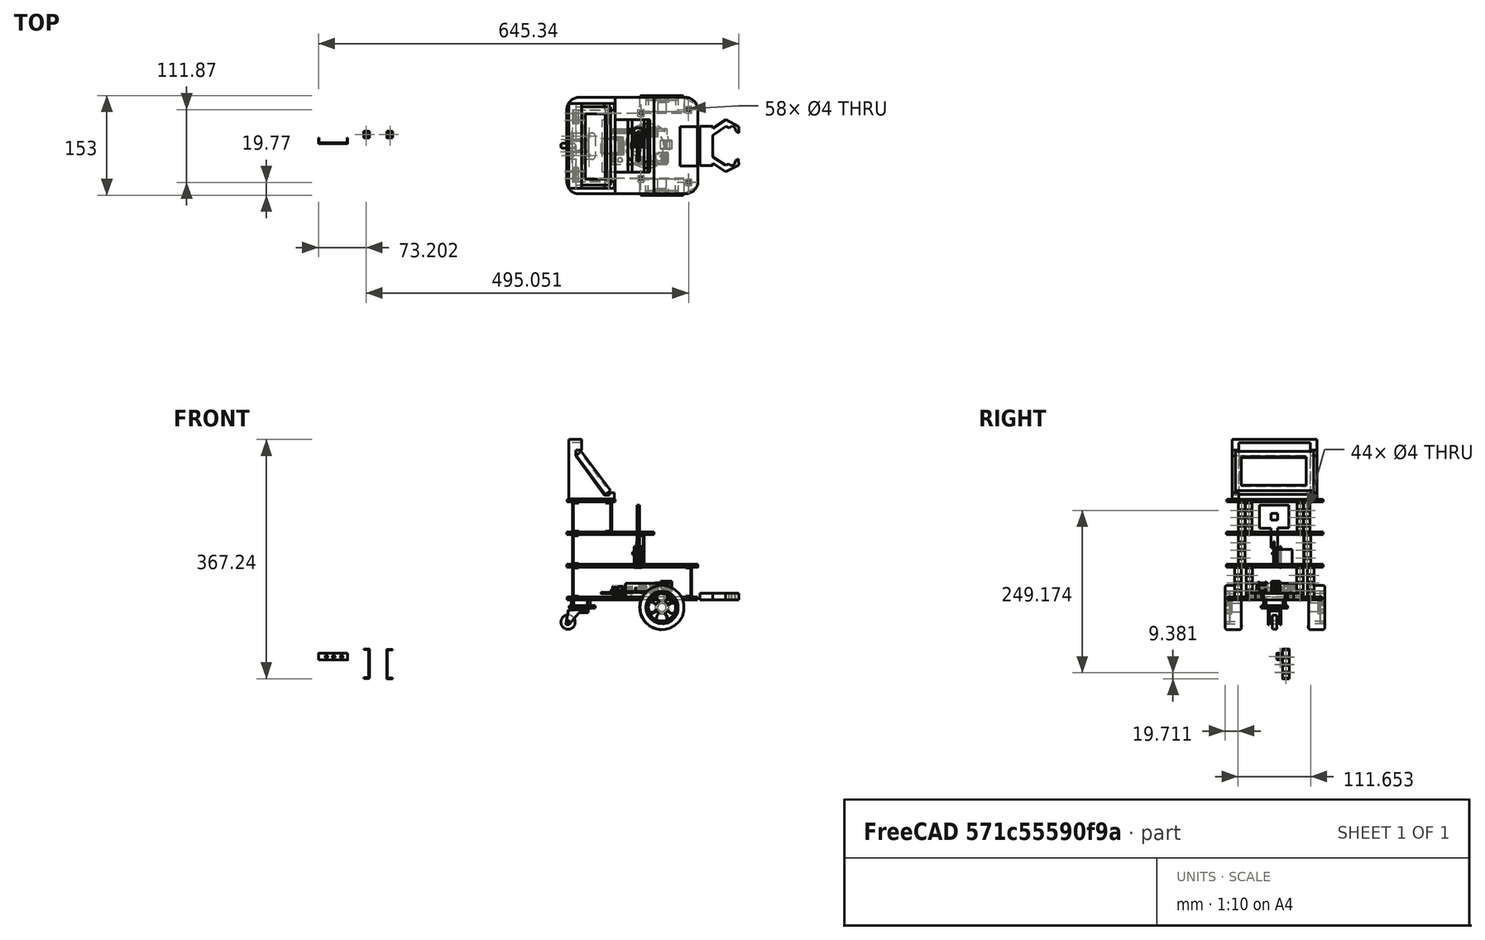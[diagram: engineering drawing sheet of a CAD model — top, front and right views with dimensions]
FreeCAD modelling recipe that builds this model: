
FCSTD DOCUMENT
Label: robot
objects: Part::Feature×53, Part::Cylinder×29, Part::Cut×29, Sketcher::SketchObject×12, PartDesign::Pad×11, App::DocumentObjectGroup×11, Part::MultiFuse×7, Part::Box×7, Part::Fillet×3, Mesh::Feature×1
note: 162 computed .brp shape members not serialized (recipe doc carries the construction recipe); baked Part::Feature solids carry a one-line shape summary decoded from their .brp

FEATURE [Sketcher::SketchObject] Sketch
  sketch-geometry (28):
    g0: LineSegment StartX=-101.13 StartY=50 StartZ=0 EndX=56.3229 EndY=50 EndZ=0
    g1: LineSegment StartX=56.3229 StartY=-50 StartZ=0 EndX=-101.13 EndY=-50 EndZ=0
    g2: LineSegment StartX=-123.405 StartY=-27.7251 StartZ=0 EndX=-123.405 EndY=27.7251 EndZ=0
    g3: ArcOfCircle CenterX=-101.13 CenterY=27.7251 CenterZ=0 NormalX=0 NormalY=0 NormalZ=1 Radius=22.2749 StartAngle=1.5708 EndAngle=3.14159
    g4: ArcOfCircle CenterX=-101.13 CenterY=-27.7251 CenterZ=0 NormalX=0 NormalY=0 NormalZ=1 Radius=22.2749 StartAngle=3.14159 EndAngle=4.71239
    g5: LineSegment StartX=6.49 StartY=27.5 StartZ=0 EndX=26.49 EndY=27.5 EndZ=0
    g6: LineSegment StartX=26.49 StartY=27.5 StartZ=0 EndX=26.49 EndY=22.5 EndZ=0
    g7: LineSegment StartX=26.49 StartY=22.5 StartZ=0 EndX=6.49 EndY=22.5 EndZ=0
    g8: LineSegment StartX=6.49 StartY=22.5 StartZ=0 EndX=6.49 EndY=27.5 EndZ=0
    g9: LineSegment StartX=6.49 StartY=-22.5 StartZ=0 EndX=26.49 EndY=-22.5 EndZ=0
    g10: LineSegment StartX=26.49 StartY=-22.5 StartZ=0 EndX=26.49 EndY=-27.5 EndZ=0
    g11: LineSegment StartX=26.49 StartY=-27.5 StartZ=0 EndX=6.49 EndY=-27.5 EndZ=0
    g12: LineSegment StartX=6.49 StartY=-27.5 StartZ=0 EndX=6.49 EndY=-22.5 EndZ=0
    g13: Circle CenterX=-115.043 CenterY=15 CenterZ=0 NormalX=0 NormalY=0 NormalZ=1 Radius=2
    g14: Circle CenterX=-115.043 CenterY=-15 CenterZ=0 NormalX=0 NormalY=0 NormalZ=1 Radius=2
    g15: Circle CenterX=-90.0431 CenterY=15 CenterZ=0 NormalX=0 NormalY=0 NormalZ=1 Radius=2
    g16: Circle CenterX=-90.0431 CenterY=-15 CenterZ=0 NormalX=0 NormalY=0 NormalZ=1 Radius=2
    g17: Circle CenterX=-109.936 CenterY=-38.9718 CenterZ=0 NormalX=0 NormalY=0 NormalZ=1 Radius=2
    g18: Circle CenterX=-109.936 CenterY=38.9718 CenterZ=0 NormalX=0 NormalY=0 NormalZ=1 Radius=2
    g19: Circle CenterX=62.653 CenterY=55.5053 CenterZ=0 NormalX=0 NormalY=0 NormalZ=1 Radius=2
    g20: Circle CenterX=62.6558 CenterY=-55.7448 CenterZ=0 NormalX=0 NormalY=0 NormalZ=1 Radius=2
    g21: LineSegment StartX=56.3229 StartY=50 StartZ=0 EndX=56.3229 EndY=73.4411 EndZ=0
    g22: LineSegment StartX=56.3229 StartY=73.4411 StartZ=0 EndX=71.7147 EndY=65.2083 EndZ=0
    g23: LineSegment StartX=76.7067 StartY=56.8801 StartZ=0 EndX=76.7456 EndY=-57.0322 EndZ=0
    g24: LineSegment StartX=71.4963 StartY=-65.4994 StartZ=0 EndX=56.3229 EndY=-73.027 EndZ=0
    g25: LineSegment StartX=56.3229 StartY=-73.027 StartZ=0 EndX=56.3229 EndY=-50 EndZ=0
    g26: ArcOfCircle CenterX=67.2972 CenterY=-57.0354 CenterZ=0 NormalX=0 NormalY=0 NormalZ=1 Radius=9.44836 StartAngle=5.17292 EndAngle=6.28353
    g27: ArcOfCircle CenterX=67.2584 CenterY=56.8768 CenterZ=0 NormalX=0 NormalY=0 NormalZ=1 Radius=9.44836 StartAngle=0.000340973 EndAngle=1.07963
  constraints (66):
    c: Horizontal(g0)
    c: Horizontal(g1)
    c: Vertical(g2)
    c: Tangent(g0,g3)
    c: Tangent(g2,g3)
    c: Tangent(g1,g4)
    c: Tangent(g2,g4)
    c: Equal(g4,g3)
    c: Symmetric(g3,g4,g4)
    c: Coincident(g5,g6)
    c: Coincident(g6,g7)
    c: Coincident(g7,g8)
    c: Coincident(g8,g5)
    c: Horizontal(g5)
    c: Horizontal(g7)
    c: Vertical(g6)
    c: Vertical(g8)
    c: Coincident(g9,g10)
    c: Coincident(g10,g11)
    c: Coincident(g11,g12)
    c: Coincident(g12,g9)
    c: Horizontal(g9)
    c: Horizontal(g11)
    c: Vertical(g10)
    c: Vertical(g12)
    c: Equal(g9,g7)
    c: Equal(g10,g6)
    c: DistanceY(g9,g6) = 45
    c: Symmetric(g7,g9,g4)
    c: DistanceY(g11,g9) = 5
    c: Distance(g9,g2) = 130
    c: DistanceX(g5,g5) = 20
    c: Equal(g14,g13)
    c: Equal(g13,g15)
    c: Equal(g15,g16)
    c: Equal(g16,g17)
    c: Equal(g17,g18)
    c: Equal(g18,g19)
    c: Equal(g19,g20)
    c: Radius(g16) = 2
    c: Symmetric(g14,g13,g4)
    c: Symmetric(g15,g16,g4)
    c: Symmetric(g18,g17,g4)
    c: Symmetric(g20,g19,g4)
    c: DistanceY(g13,g14) = -30
    c: DistanceX(g15,g13) = -25
    c: DistanceY(g16,g15) = 30
    c: DistanceX(g14) = -115.043
    c: DistanceX(g17) = -109.936
    c: DistanceY(g17,g18) = 77.9436
    c: Coincident(g21,g0)
    c: Coincident(g21,g22)
    c: Coincident(g24,g25)
    c: Coincident(g25,g1)
    c: Tangent(g23,g26)
    c: Tangent(g24,g26)
    c: Tangent(g22,g27)
    c: Tangent(g23,g27)
    c: Equal(g27,g26)
    c: Symmetric(g21,g24,g3)
    c: Symmetric(g26,g27,g3)
    c: DistanceY(g0) = 50
    c: DistanceY(g0,g1) = -100
    c: Symmetric(g20,g19,g3)
    c: Vertical(g25)
    c: Vertical(g21)
FEATURE [Sketcher::SketchObject] Sketch001
  sketch-geometry (31):
    g0: LineSegment StartX=-104.318 StartY=74.4003 StartZ=0 EndX=57.597 EndY=74.4003 EndZ=0
    g1: LineSegment StartX=57.7487 StartY=-73.8607 StartZ=0 EndX=-104.318 EndY=-73.8607 EndZ=0
    g2: LineSegment StartX=-124.085 StartY=-54.0935 StartZ=0 EndX=-124.085 EndY=54.6331 EndZ=0
    g3: LineSegment [constr] StartX=-124.085 StartY=-0.458382 StartZ=0 EndX=-29.7491 EndY=-0.458382 EndZ=0
    g4: Circle CenterX=-110.299 CenterY=39.0839 CenterZ=0 NormalX=0 NormalY=0 NormalZ=1 Radius=2
    g5: Circle CenterX=-109.764 CenterY=-38.9049 CenterZ=0 NormalX=0 NormalY=0 NormalZ=1 Radius=2
    g6: Circle CenterX=62.7977 CenterY=55.4219 CenterZ=0 NormalX=0 NormalY=0 NormalZ=1 Radius=2
    g7: Circle CenterX=62.9826 CenterY=-55.9466 CenterZ=0 NormalX=0 NormalY=0 NormalZ=1 Radius=2
    g8: ArcOfCircle CenterX=-104.318 CenterY=54.6331 CenterZ=0 NormalX=0 NormalY=0 NormalZ=1 Radius=19.7672 StartAngle=1.5708 EndAngle=3.14159
    g9: ArcOfCircle CenterX=-104.318 CenterY=-54.0935 CenterZ=0 NormalX=0 NormalY=0 NormalZ=1 Radius=19.7672 StartAngle=3.14159 EndAngle=4.71239
    g10: ArcOfCircle CenterX=57.597 CenterY=54.6331 CenterZ=0 NormalX=0 NormalY=0 NormalZ=1 Radius=19.7672 StartAngle=6.22162 EndAngle=7.85398
    g11: ArcOfCircle CenterX=57.7487 CenterY=-54.0935 CenterZ=0 NormalX=0 NormalY=0 NormalZ=1 Radius=19.7672 StartAngle=4.71239 EndAngle=6.14475
    g12: LineSegment StartX=77.3268 StartY=29.3887 StartZ=0 EndX=50.0396 EndY=29.3887 EndZ=0
    g13: LineSegment StartX=50.0396 StartY=29.3887 StartZ=0 EndX=50.0396 EndY=-30.714 EndZ=0
    g14: LineSegment StartX=77.3268 StartY=-56.8212 StartZ=0 EndX=77.3268 EndY=-30.714 EndZ=0
    g15: LineSegment StartX=77.3268 StartY=29.3887 StartZ=0 EndX=77.3268 EndY=53.4168 EndZ=0
    g16: Circle CenterX=-110.008 CenterY=-50.2945 CenterZ=0 NormalX=0 NormalY=0 NormalZ=1 Radius=2
    g17: Circle CenterX=-110.008 CenterY=49.3777 CenterZ=0 NormalX=0 NormalY=0 NormalZ=1 Radius=2
    g18: Circle CenterX=-10.1147 CenterY=50.2419 CenterZ=0 NormalX=0 NormalY=0 NormalZ=1 Radius=2
    g19: Circle CenterX=-10.1344 CenterY=-50.6043 CenterZ=0 NormalX=0 NormalY=0 NormalZ=1 Radius=2
    g20: LineSegment StartX=-29.7491 StartY=40.2702 StartZ=0 EndX=-23.9444 EndY=40.2702 EndZ=0
    g21: LineSegment StartX=-23.9444 StartY=40.2702 StartZ=0 EndX=-23.9444 EndY=-40.2702 EndZ=0
    g22: LineSegment StartX=-23.9444 StartY=-40.2702 StartZ=0 EndX=-29.7491 EndY=-40.2702 EndZ=0
    g23: LineSegment StartX=-29.7491 StartY=-40.2702 StartZ=0 EndX=-29.7491 EndY=40.2702 EndZ=0
    g24: LineSegment StartX=-5.44191 StartY=40.2702 StartZ=0 EndX=0.362807 EndY=40.2702 EndZ=0
    g25: LineSegment StartX=0.362807 StartY=40.2702 StartZ=0 EndX=0.362807 EndY=-40.2702 EndZ=0
    g26: LineSegment StartX=0.362807 StartY=-40.2702 StartZ=0 EndX=-5.44191 EndY=-40.2702 EndZ=0
    g27: LineSegment StartX=-5.44191 StartY=-40.2702 StartZ=0 EndX=-5.44191 EndY=40.2702 EndZ=0
    g28: LineSegment [constr] StartX=-23.9444 StartY=-0.458382 StartZ=0 EndX=-5.44191 EndY=-0.458382 EndZ=0
    g29: LineSegment [constr] StartX=50.0396 StartY=-0.458382 StartZ=0 EndX=76.3643 EndY=-0.458382 EndZ=0
    g30: LineSegment StartX=77.3268 StartY=-30.714 StartZ=0 EndX=50.0396 EndY=-30.714 EndZ=0
  constraints (45):
    c: Horizontal(g0)
    c: Horizontal(g1)
    c: Vertical(g2)
    c: PointOnObject(g3,g2)
    c: Equal(g5,g4)
    c: Equal(g4,g6)
    c: Equal(g6,g7)
    c: Radius(g5) = 2
    c: Tangent(g0,g8)
    c: Tangent(g2,g8)
    c: Tangent(g1,g9)
    c: Tangent(g2,g9)
    c: Tangent(g0,g10)
    c: Tangent(g1,g11)
    c: Horizontal(g12)
    c: Coincident(g12,g13)
    c: Vertical(g13)
    c: Coincident(g14,g11)
    c: Vertical(g14)
    c: Coincident(g15,g12)
    c: Coincident(g15,g10)
    c: Vertical(g15)
    c: Equal(g16,g17)
    c: Radius(g16) = 2
    c: Radius(g18) = 2
    c: Coincident(g20,g21)
    c: Coincident(g21,g22)
    c: Coincident(g22,g23)
    c: Coincident(g23,g20)
    c: Horizontal(g20)
    c: Horizontal(g22)
    c: Coincident(g24,g25)
    c: Coincident(g25,g26)
    c: Coincident(g26,g27)
    c: Coincident(g27,g24)
    c: Horizontal(g24)
    c: Horizontal(g26)
    c: Symmetric(g16,g17,g3)
    c: Tangent(g3,g28)
    c: PointOnObject(g29,g13)
    c: Tangent(g28,g29)
    c: PointOnObject(g28,g27)
    c: Coincident(g30,g14)
    c: Coincident(g30,g13)
    c: Horizontal(g30)
FEATURE [PartDesign::Pad] Pad001
  Length = 4
  MirroredExtent = false
  Placement = pos=(0,0,50) rot=(0,0,1;0rad)
  Sketch = -> Sketch001
FEATURE [Sketcher::SketchObject] Sketch002
  sketch-geometry (18):
    g0: LineSegment StartX=-104.405 StartY=74.3817 StartZ=0 EndX=9.85074 EndY=74.3817 EndZ=0
    g1: LineSegment StartX=9.85074 StartY=74.3817 StartZ=0 EndX=9.85074 EndY=-73.7972 EndZ=0
    g2: LineSegment StartX=9.85074 StartY=-73.7972 StartZ=0 EndX=-104.405 EndY=-73.7972 EndZ=0
    g3: LineSegment StartX=-123.988 StartY=-54.214 StartZ=0 EndX=-123.988 EndY=54.7984 EndZ=0
    g4: ArcOfCircle CenterX=-104.405 CenterY=54.7984 CenterZ=0 NormalX=0 NormalY=0 NormalZ=1 Radius=19.5832 StartAngle=1.5708 EndAngle=3.14159
    g5: ArcOfCircle CenterX=-104.405 CenterY=-54.214 CenterZ=0 NormalX=0 NormalY=0 NormalZ=1 Radius=19.5832 StartAngle=3.14159 EndAngle=4.71239
    g6: Circle CenterX=-109.932 CenterY=49.3917 CenterZ=0 NormalX=0 NormalY=0 NormalZ=1 Radius=2
    g7: Circle CenterX=-110.012 CenterY=-50.1232 CenterZ=0 NormalX=0 NormalY=0 NormalZ=1 Radius=2
    g8: Circle CenterX=-9.94777 CenterY=50.1271 CenterZ=0 NormalX=0 NormalY=0 NormalZ=1 Radius=2
    g9: Circle CenterX=-10.198 CenterY=-50.2781 CenterZ=0 NormalX=0 NormalY=0 NormalZ=1 Radius=2
    g10: LineSegment StartX=-69.6455 StartY=40.3214 StartZ=0 EndX=3.40336 EndY=40.3214 EndZ=0
    g11: LineSegment StartX=3.40336 StartY=40.3214 StartZ=0 EndX=3.40336 EndY=-40.303 EndZ=0
    g12: LineSegment StartX=3.40336 StartY=-40.303 StartZ=0 EndX=-69.6455 EndY=-40.303 EndZ=0
    g13: LineSegment StartX=-69.6455 StartY=-40.303 StartZ=0 EndX=-69.6455 EndY=40.3214 EndZ=0
    g14: Circle CenterX=-109.839 CenterY=39.7373 CenterZ=0 NormalX=0 NormalY=0 NormalZ=1 Radius=2
    g15: Circle CenterX=-110.415 CenterY=-39.9994 CenterZ=0 NormalX=0 NormalY=0 NormalZ=1 Radius=2
    g16: Circle CenterX=-59.5193 CenterY=-50.2572 CenterZ=0 NormalX=0 NormalY=0 NormalZ=1 Radius=2
    g17: Circle CenterX=-60.2629 CenterY=49.9665 CenterZ=0 NormalX=0 NormalY=0 NormalZ=1 Radius=2
  constraints (27):
    c: Coincident(g0,g1)
    c: Coincident(g1,g2)
    c: Horizontal(g0)
    c: Horizontal(g2)
    c: Vertical(g1)
    c: Vertical(g3)
    c: Tangent(g0,g4)
    c: Tangent(g3,g4)
    c: Tangent(g2,g5)
    c: Tangent(g3,g5)
    c: Equal(g4,g5)
    c: Equal(g6,g7)
    c: Equal(g7,g9)
    c: Equal(g9,g8)
    c: Radius(g6) = 2
    c: Coincident(g10,g11)
    c: Coincident(g11,g12)
    c: Coincident(g12,g13)
    c: Coincident(g13,g10)
    c: Horizontal(g10)
    c: Horizontal(g12)
    c: Vertical(g11)
    c: Vertical(g13)
    c: Equal(g15,g14)
    c: Equal(g14,g17)
    c: Equal(g17,g16)
    c: Radius(g15) = 2
FEATURE [PartDesign::Pad] Pad002
  Length = 4
  MirroredExtent = false
  Placement = pos=(0,0,100) rot=(0,0,1;0rad)
  Sketch = -> Sketch002
FEATURE [Sketcher::SketchObject] Sketch003
  sketch-geometry (12):
    g0: ArcOfCircle CenterX=-105.074 CenterY=55.6821 CenterZ=0 NormalX=0 NormalY=0 NormalZ=1 Radius=18.6332 StartAngle=1.60655 EndAngle=3.14159
    g1: ArcOfCircle CenterX=-105.346 CenterY=-55.3418 CenterZ=0 NormalX=0 NormalY=0 NormalZ=1 Radius=18.3958 StartAngle=3.20271 EndAngle=4.69093
    g2: LineSegment StartX=-50.0043 StartY=74.3033 StartZ=0 EndX=-50.0043 EndY=-73.7333 EndZ=0
    g3: LineSegment StartX=-105.74 StartY=74.3033 StartZ=0 EndX=-50.0043 EndY=74.3033 EndZ=0
    g4: LineSegment StartX=-105.741 StartY=-73.7333 StartZ=0 EndX=-50.0043 EndY=-73.7333 EndZ=0
    g5: Circle CenterX=-109.743 CenterY=39.5908 CenterZ=0 NormalX=0 NormalY=0 NormalZ=1 Radius=2
    g6: Circle CenterX=-110.279 CenterY=-40.0459 CenterZ=0 NormalX=0 NormalY=0 NormalZ=1 Radius=2
    g7: Circle CenterX=-60.203 CenterY=49.9128 CenterZ=0 NormalX=0 NormalY=0 NormalZ=1 Radius=2
    g8: Circle CenterX=-59.3002 CenterY=-50.3702 CenterZ=0 NormalX=0 NormalY=0 NormalZ=1 Radius=2
    g9: Circle CenterX=-116.132 CenterY=9.74953 CenterZ=0 NormalX=0 NormalY=0 NormalZ=1 Radius=2
    g10: Circle CenterX=-116.544 CenterY=-9.66085 CenterZ=0 NormalX=0 NormalY=0 NormalZ=1 Radius=2
    g11: LineSegment StartX=-123.707 StartY=55.6821 StartZ=0 EndX=-123.707 EndY=-56.4655 EndZ=0
  constraints (17):
    c: Coincident(g3,g0)
    c: Coincident(g3,g2)
    c: Coincident(g4,g1)
    c: Coincident(g4,g2)
    c: Equal(g6,g5)
    c: Equal(g5,g7)
    c: Equal(g7,g8)
    c: Radius(g6) = 2
    c: Horizontal(g3)
    c: Vertical(g2)
    c: Horizontal(g4)
    c: Equal(g10,g9)
    c: Radius(g9) = 2
    c: Coincident(g11,g0)
    c: Coincident(g11,g1)
    c: Vertical(g11)
    c: Tangent(g11,g0)
FEATURE [PartDesign::Pad] Pad003
  Length = 4
  MirroredExtent = false
  Placement = pos=(0,0,150) rot=(0,0,1;0rad)
  Sketch = -> Sketch003
FEATURE [Part::Cylinder] Cylinder005
  Angle = 360
  Height = 25
  Radius = 6.5
FEATURE [Part::Cylinder] Cylinder006
  Angle = 360
  Height = 10
  Radius = 10
FEATURE [Part::Cylinder] Cylinder010
  Angle = 360
  Height = 7
  Placement = pos=(0.664718,-16.3626,0) rot=(0,0,1;0rad)
  Radius = 8
FEATURE [Part::Cylinder] Cylinder011
  Angle = 360
  Height = 7
  Placement = pos=(16.4955,0.685902,0) rot=(0,0,1;0rad)
  Radius = 8
FEATURE [Part::Cylinder] Cylinder012
  Angle = 360
  Height = 7
  Placement = pos=(-16.3838,-1.44516,0) rot=(0,0,1;0rad)
  Radius = 8
FEATURE [Part::Cylinder] Cylinder013
  Angle = 360
  Height = 25
  Radius = 25
FEATURE [Part::Cylinder] Cylinder009
  Angle = 360
  Height = 7
  Placement = pos=(-0.248596,16.2122,0) rot=(0,0,1;0rad)
  Radius = 8
FEATURE [Part::MultiFuse] Fusion
  Placement = pos=(22,77,-12) rot=(1,0,0;1.5708rad)
  Shapes = -> [Cylinder006,Cylinder011,Cylinder012,Cylinder010,Cylinder009,Cylinder005]
FEATURE [Part::Cylinder] Cylinder014
  Angle = 360
  Height = 25
  Radius = 34
FEATURE [Part::Cylinder] Cylinder015
  Angle = 360
  Height = 25
  Radius = 21
FEATURE [Part::Cylinder] Cylinder016
  Angle = 360
  Height = 25
  Radius = 25
FEATURE [Part::Cut] Cut002
  Base = -> Cylinder016
  Placement = pos=(22,77,-12) rot=(1,0,0;1.5708rad)
  Tool = -> Cylinder015
FEATURE [Part::Fillet] Fillet
  Edges = 2 edges r=3: [Edge2,Edge3]
  Placement = pos=(22,77,-12) rot=(1,0,0;1.5708rad)
FEATURE [App::DocumentObjectGroup] Group  label="wheel"
  Group = -> [Cut002,Fusion,Fillet]
FEATURE [Part::Cylinder] Cylinder
  Angle = 360
  Height = 7
  Radius = 11
FEATURE [Part::Cylinder] Cylinder017
  Angle = 360
  Height = 7
  Radius = 2.5
FEATURE [Part::Cut] Cut
  Base = -> Cylinder
  Tool = -> Cylinder017
FEATURE [Part::Fillet] Fillet001
  Base = -> Cut
  Edges = 4 edges r=2: [Edge1,Edge3,Edge4,Edge5]
  Placement = pos=(-122,-3.4,-34.5) rot=(0,0.707107,0.707107;3.14159rad)
FEATURE [App::DocumentObjectGroup] Group001  label="wheel0"
  Group = -> [Cylinder017,Cylinder,Fillet001]
FEATURE [Sketcher::SketchObject] Sketch004
  sketch-geometry (11):
    g0: LineSegment StartX=-39.5249 StartY=-0.0489382 StartZ=0 EndX=-9.52487 EndY=-0.0489382 EndZ=0
    g1: LineSegment StartX=-9.52487 StartY=-0.0489382 StartZ=0 EndX=-5.3256 EndY=-21.3647 EndZ=0
    g2: LineSegment StartX=-6.46484 StartY=-22.7502 StartZ=0 EndX=-9.08519 EndY=-22.7502 EndZ=0
    g3: LineSegment StartX=-10.2117 StartY=-22.2424 StartZ=0 EndX=-25.3922 EndY=-5.06478 EndZ=0
    g4: LineSegment StartX=-27.2038 StartY=-4.24812 StartZ=0 EndX=-38.567 EndY=-4.24812 EndZ=0
    g5: LineSegment StartX=-39.5249 StartY=-3.29027 StartZ=0 EndX=-39.5249 EndY=-0.0489382 EndZ=0
    g6: ArcOfCircle CenterX=-6.46484 CenterY=-21.5891 CenterZ=0 NormalX=0 NormalY=0 NormalZ=1 Radius=1.16114 StartAngle=4.71239 EndAngle=6.4777
    g7: ArcOfCircle CenterX=-9.08519 CenterY=-21.2469 CenterZ=0 NormalX=0 NormalY=0 NormalZ=1 Radius=1.50333 StartAngle=3.86535 EndAngle=4.71239
    g8: ArcOfCircle CenterX=-27.2038 CenterY=-6.66574 CenterZ=0 NormalX=0 NormalY=0 NormalZ=1 Radius=2.41762 StartAngle=0.723759 EndAngle=1.5708
    g9: Circle CenterX=-8.87657 CenterY=-18.7194 CenterZ=0 NormalX=0 NormalY=0 NormalZ=1 Radius=2
    g10: ArcOfCircle CenterX=-38.567 CenterY=-3.29027 CenterZ=0 NormalX=0 NormalY=0 NormalZ=1 Radius=0.95785 StartAngle=3.14159 EndAngle=4.71239
  constraints (16):
    c: Horizontal(g0)
    c: Distance(g0) = 30
    c: Coincident(g1,g0)
    c: Horizontal(g2)
    c: Horizontal(g4)
    c: Coincident(g5,g0)
    c: Vertical(g5)
    c: Tangent(g1,g6)
    c: Tangent(g2,g6)
    c: Tangent(g2,g7)
    c: Tangent(g3,g7)
    c: Tangent(g3,g8)
    c: Tangent(g4,g8)
    c: Radius(g9) = 2
    c: Tangent(g4,g10)
    c: Tangent(g5,g10)
FEATURE [PartDesign::Pad] Pad004
  Length = 20
  MirroredExtent = false
  Placement = pos=(40,27,-2) rot=(0,0,1;0rad)
  Sketch = -> Sketch004
FEATURE [Part::Box] Box
  Height = 16
  Length = 40
  Width = 25
FEATURE [Part::Cut] Cut003
  Base = -> Pad004
  Placement = pos=(-90.7,-8,-42.5) rot=(0,0.707107,0.707107;3.14159rad)
  Tool = -> Box
FEATURE [App::DocumentObjectGroup] Group002  label="wl"
  Group = -> [Cut003]
FEATURE [Part::Fillet] Fillet002
  Edges = 2 edges r=3: [Edge2,Edge3]
  Placement = pos=(22.3,-76,-12) rot=(0,0.707107,0.707107;3.14159rad)
FEATURE [Part::MultiFuse] Fusion001
  Placement = pos=(22.3,-76,-12) rot=(0,0.707107,0.707107;3.14159rad)
  Shapes = -> [Cylinder006,Cylinder011,Cylinder012,Cylinder010,Cylinder009,Cylinder005]
FEATURE [Part::Cut] Cut004
  Base = -> Cylinder016
  Placement = pos=(22.3,-76,-12) rot=(0,0.707107,0.707107;3.14159rad)
  Tool = -> Cylinder015
FEATURE [App::DocumentObjectGroup] Group003  label="wheel01"
  Group = -> [Cut004,Fusion001,Fillet002]
FEATURE [App::DocumentObjectGroup] Group004
FEATURE [Sketcher::SketchObject] Sketch005  label="Sketch_plate"
  sketch-geometry (12):
    g0: LineSegment StartX=-114.888 StartY=19.7983 StartZ=0 EndX=-85.6217 EndY=19.7983 EndZ=0
    g1: LineSegment StartX=-80.1008 StartY=14.2774 StartZ=0 EndX=-80.1008 EndY=-15.4701 EndZ=0
    g2: LineSegment StartX=-85.6217 StartY=-20.991 StartZ=0 EndX=-114.888 EndY=-20.991 EndZ=0
    g3: LineSegment StartX=-120.409 StartY=-15.4701 StartZ=0 EndX=-120.409 EndY=14.2774 EndZ=0
    g4: Circle CenterX=-115.076 CenterY=14.931 CenterZ=0 NormalX=0 NormalY=0 NormalZ=1 Radius=2
    g5: Circle CenterX=-115.258 CenterY=-14.9052 CenterZ=0 NormalX=0 NormalY=0 NormalZ=1 Radius=2
    g6: Circle CenterX=-90.0087 CenterY=14.931 CenterZ=0 NormalX=0 NormalY=0 NormalZ=1 Radius=2
    g7: Circle CenterX=-89.8897 CenterY=-14.9413 CenterZ=0 NormalX=0 NormalY=0 NormalZ=1 Radius=2
    g8: ArcOfCircle CenterX=-85.6217 CenterY=14.2774 CenterZ=0 NormalX=0 NormalY=0 NormalZ=1 Radius=5.52093 StartAngle=0 EndAngle=1.5708
    g9: ArcOfCircle CenterX=-85.6217 CenterY=-15.4701 CenterZ=0 NormalX=0 NormalY=0 NormalZ=1 Radius=5.52093 StartAngle=4.71239 EndAngle=6.28319
    g10: ArcOfCircle CenterX=-114.888 CenterY=14.2774 CenterZ=0 NormalX=0 NormalY=0 NormalZ=1 Radius=5.52093 StartAngle=1.5708 EndAngle=3.14159
    g11: ArcOfCircle CenterX=-114.888 CenterY=-15.4701 CenterZ=0 NormalX=0 NormalY=0 NormalZ=1 Radius=5.52093 StartAngle=3.14159 EndAngle=4.71239
  constraints (19):
    c: Horizontal(g0)
    c: Horizontal(g2)
    c: Vertical(g1)
    c: Vertical(g3)
    c: Equal(g4,g5)
    c: Equal(g5,g7)
    c: Equal(g7,g6)
    c: Radius(g6) = 2
    c: Tangent(g0,g8)
    c: Tangent(g1,g8)
    c: Tangent(g1,g9)
    c: Tangent(g2,g9)
    c: Tangent(g0,g10)
    c: Tangent(g3,g10)
    c: Tangent(g2,g11)
    c: Tangent(g3,g11)
    c: Equal(g11,g10)
    c: Equal(g10,g8)
    c: Equal(g8,g9)
FEATURE [PartDesign::Pad] Pad
  Length = 4
  MirroredExtent = false
  Sketch = -> Sketch
FEATURE [PartDesign::Pad] Pad005
  Length = 4
  MirroredExtent = false
  Placement = pos=(0,0,-13) rot=(0,0,1;0rad)
  Sketch = -> Sketch005
FEATURE [Part::Cylinder] Cylinder018
  Angle = 360
  Height = 4
  Placement = pos=(-107,0,-16) rot=(0,0,1;0rad)
  Radius = 7
FEATURE [Part::Cylinder] Cylinder019
  Angle = 360
  Height = 10
  Placement = pos=(-115.055,-14.9752,-9) rot=(0,0,1;0rad)
  Radius = 2
FEATURE [Part::Cylinder] Cylinder020
  Angle = 360
  Height = 10
  Placement = pos=(-90.0431,-15,-10) rot=(0,0,1;0rad)
  Radius = 2
FEATURE [Part::Cylinder] Cylinder021
  Angle = 360
  Height = 10
  Placement = pos=(-89.9511,14.932,-10) rot=(0,0,1;0rad)
  Radius = 2
FEATURE [Part::Cylinder] Cylinder022
  Angle = 360
  Height = 10
  Placement = pos=(-115.109,14.8885,-9) rot=(0,0,1;0rad)
  Radius = 2
FEATURE [Sketcher::SketchObject] Sketch006
  sketch-geometry (15):
    g0: LineSegment StartX=-29.9116 StartY=5.05926 StartZ=0 EndX=30.0884 EndY=5.05926 EndZ=0
    g1: LineSegment StartX=34.7894 StartY=0.358325 StartZ=0 EndX=34.7894 EndY=-0.239814 EndZ=0
    g2: LineSegment StartX=30.0884 StartY=-4.94074 StartZ=0 EndX=-29.9116 EndY=-4.94074 EndZ=0
    g3: LineSegment StartX=-34.6125 StartY=-0.239814 StartZ=0 EndX=-34.6125 EndY=0.358325 EndZ=0
    g4: ArcOfCircle CenterX=-29.9116 CenterY=0.358325 CenterZ=0 NormalX=0 NormalY=0 NormalZ=1 Radius=4.70093 StartAngle=1.5708 EndAngle=3.14159
    g5: ArcOfCircle CenterX=-29.9116 CenterY=-0.239814 CenterZ=0 NormalX=0 NormalY=0 NormalZ=1 Radius=4.70093 StartAngle=3.14159 EndAngle=4.71239
    g6: ArcOfCircle CenterX=30.0884 CenterY=0.358325 CenterZ=0 NormalX=0 NormalY=0 NormalZ=1 Radius=4.70093 StartAngle=0 EndAngle=1.5708
    g7: ArcOfCircle CenterX=30.0884 CenterY=-0.239814 CenterZ=0 NormalX=0 NormalY=0 NormalZ=1 Radius=4.70093 StartAngle=4.71239 EndAngle=6.28319
    g8: Circle CenterX=-29.9299 CenterY=0.0119776 CenterZ=0 NormalX=0 NormalY=0 NormalZ=1 Radius=2
    g9: Circle CenterX=-11.1706 CenterY=0.0385086 CenterZ=0 NormalX=0 NormalY=0 NormalZ=1 Radius=2
    g10: Circle CenterX=11.1127 CenterY=-0.0115485 CenterZ=0 NormalX=0 NormalY=0 NormalZ=1 Radius=2
    g11: Circle CenterX=0.0455946 CenterY=-0.112972 CenterZ=0 NormalX=0 NormalY=0 NormalZ=1 Radius=2
    g12: Circle CenterX=30.0576 CenterY=0.117842 CenterZ=0 NormalX=0 NormalY=0 NormalZ=1 Radius=2
    g13: LineSegment StartX=25.3875 StartY=-4.94074 StartZ=0 EndX=25.3875 EndY=5.05926 EndZ=0
    g14: LineSegment StartX=-25.2106 StartY=-4.94074 StartZ=0 EndX=-25.2106 EndY=5.05926 EndZ=0
  constraints (30):
    c: Horizontal(g0)
    c: Horizontal(g2)
    c: Vertical(g1)
    c: Vertical(g3)
    c: Tangent(g0,g4)
    c: Tangent(g3,g4)
    c: Tangent(g2,g5)
    c: Tangent(g3,g5)
    c: Tangent(g0,g6)
    c: Tangent(g1,g6)
    c: Tangent(g1,g7)
    c: Tangent(g2,g7)
    c: Equal(g4,g5)
    c: Equal(g5,g6)
    c: Equal(g6,g7)
    c: Distance(g2) = 60
    c: DistanceY(g0,g2) = -10
    c: Equal(g8,g9)
    c: Equal(g9,g10)
    c: Equal(g10,g11)
    c: Equal(g11,g12)
    c: Radius(g8) = 2
    c: PointOnObject(g13,g2)
    c: PointOnObject(g13,g0)
    c: Vertical(g13)
    c: Tangent(g13,g6)
    c: PointOnObject(g14,g2)
    c: PointOnObject(g14,g0)
    c: Vertical(g14)
    c: Tangent(g14,g4)
FEATURE [Sketcher::SketchObject] Sketch007
  sketch-geometry (12):
    g0: LineSegment StartX=20.5461 StartY=-1.20827 StartZ=0 EndX=-22.4155 EndY=-1.20827 EndZ=0
    g1: LineSegment StartX=-23.4007 StartY=7.77698 StartZ=0 EndX=-22.4007 EndY=7.77698 EndZ=0
    g2: LineSegment StartX=-22.4007 StartY=7.77698 StartZ=0 EndX=-22.4007 EndY=0.197829 EndZ=0
    g3: LineSegment StartX=21.5992 StartY=7.84487 StartZ=0 EndX=20.5992 EndY=7.84487 EndZ=0
    g4: LineSegment StartX=20.5992 StartY=7.84487 StartZ=0 EndX=20.5992 EndY=-0.149263 EndZ=0
    g5: LineSegment StartX=-22.0096 StartY=-0.193299 StartZ=0 EndX=20.5552 EndY=-0.193299 EndZ=0
    g6: LineSegment StartX=-23.4007 StartY=7.77698 StartZ=0 EndX=-23.4007 EndY=-0.223018 EndZ=0
    g7: LineSegment StartX=21.5992 StartY=7.84487 StartZ=0 EndX=21.5992 EndY=-0.155135 EndZ=0
    g8: ArcOfCircle CenterX=-22.4155 CenterY=-0.223018 CenterZ=0 NormalX=0 NormalY=0 NormalZ=1 Radius=0.985254 StartAngle=3.14159 EndAngle=4.71239
    g9: ArcOfCircle CenterX=20.5461 CenterY=-0.155135 CenterZ=0 NormalX=0 NormalY=0 NormalZ=1 Radius=1.05314 StartAngle=4.71239 EndAngle=6.28319
    g10: ArcOfCircle CenterX=20.5552 CenterY=-0.149263 CenterZ=0 NormalX=0 NormalY=0 NormalZ=1 Radius=0.044036 StartAngle=4.71239 EndAngle=6.28319
    g11: ArcOfCircle CenterX=-22.0096 CenterY=0.197829 CenterZ=0 NormalX=0 NormalY=0 NormalZ=1 Radius=0.391129 StartAngle=3.14159 EndAngle=4.71239
  constraints (25):
    c: Coincident(g2,g1)
    c: Vertical(g2)
    c: Coincident(g4,g3)
    c: Vertical(g4)
    c: Distance(g1) = 1
    c: Distance(g3) = 1
    c: Coincident(g6,g1)
    c: Vertical(g6)
    c: Coincident(g7,g3)
    c: Vertical(g7)
    c: Tangent(g0,g8)
    c: Tangent(g6,g8)
    c: Tangent(g0,g9)
    c: Tangent(g7,g9)
    c: Tangent(g4,g10)
    c: Tangent(g5,g10)
    c: Tangent(g2,g11)
    c: Tangent(g5,g11)
    c: Distance(g1,g3) = 43
    c: Distance(g3,g7) = 8
    c: Distance(g1,g6) = 8
    c: Horizontal(g5)
    c: Horizontal(g0)
    c: Horizontal(g1)
    c: Horizontal(g3)
FEATURE [PartDesign::Pad] Pad006
  Length = 10
  MirroredExtent = false
  Sketch = -> Sketch007
FEATURE [Part::Cylinder] Cylinder025
  Angle = 360
  Height = 2
  Placement = pos=(25,5.38,4.9) rot=(0.706319,-0.023027,0.707519;3.16911rad)
  Radius = 2
FEATURE [Part::Cylinder] Cylinder026
  Angle = 360
  Height = 2
  Placement = pos=(-26,5.29,4.9) rot=(0.706319,-0.023027,0.707519;3.16911rad)
  Radius = 2
FEATURE [Part::Cylinder] Cylinder027
  Angle = 360
  Height = 2
  Placement = pos=(12.2129,0,4.81114) rot=(1,0,0;1.5708rad)
  Radius = 2
FEATURE [Part::Cylinder] Cylinder028
  Angle = 360
  Height = 2
  Placement = pos=(-11.1555,-4.76837e-07,4.86401) rot=(1,0,0;1.5708rad)
  Radius = 2
FEATURE [Part::Cylinder] Cylinder029
  Angle = 360
  Height = 2
  Placement = pos=(-2.98023e-07,0,4.86401) rot=(1,0,0;1.5708rad)
  Radius = 2
FEATURE [Part::Cut] Cut005
  Base = -> Pad006
  Tool = -> Cylinder025
FEATURE [Part::Cut] Cut006
  Base = -> Cut005
  Tool = -> Cylinder027
FEATURE [Part::Cut] Cut007
  Base = -> Cut006
  Tool = -> Cylinder029
FEATURE [Part::Cut] Cut008
  Base = -> Cut007
  Tool = -> Cylinder028
FEATURE [Part::Cut] Cut009
  Base = -> Cut008
  Tool = -> Cylinder026
FEATURE [Part::MultiFuse] Fusion002  label="back_wheel"
  Shapes = -> [Fillet001,Pad005,Cylinder018,Cylinder019,Cylinder020,Cylinder021,Cylinder022,Cut003]
FEATURE [Part::Cylinder] Cylinder030
  Angle = 360
  Height = 10
  Placement = pos=(15.49,3.9,4.87) rot=(0,1,0;1.5708rad)
  Radius = 2
FEATURE [Part::Cylinder] Cylinder031
  Angle = 360
  Height = 10
  Placement = pos=(-28.4147,3.9,5.14) rot=(0,1,0;1.5708rad)
  Radius = 2
FEATURE [Part::Cut] Cut018
  Base = -> Cut009
  Tool = -> Cylinder031
FEATURE [Part::Cut] Cut019
  Base = -> Cut018
  Placement = pos=(-481.872,4.52656,-92.3721) rot=(0,0,1;0rad)
  Tool = -> Cylinder030
FEATURE [Part::Cut] Cut022
  Base = -> Cut018
  Placement = pos=(-428.168,12.2394,-99.0758) rot=(-0.57735,0.57735,0.57735;2.0944rad)
  Tool = -> Cylinder030
FEATURE [Part::Cut] Cut023
  Base = -> Cut018
  Placement = pos=(-399.312,22.2394,-99.8057) rot=(0.57735,0.57735,-0.57735;2.0944rad)
  Tool = -> Cylinder030
FEATURE [App::DocumentObjectGroup] Group005  label="junk"
  Group = -> [Sketch006,Group001,Group002,Group004,Cut008,Cut019,Cut022,Cut023,Cylinder014,Cylinder013]
FEATURE [Part::Cut] Cut024
  Base = -> Cut018
  Placement = pos=(-114,44,26) rot=(0.57735,0.57735,-0.57735;2.0944rad)
  Tool = -> Cylinder030
FEATURE [Part::Cut] Cut025
  Base = -> Cut018
  Placement = pos=(66.5,-61.1,26) rot=(0.57735,-0.57735,-0.57735;4.18879rad)
  Tool = -> Cylinder030
FEATURE [Part::Cut] Cut026
  Base = -> Cut018
  Placement = pos=(66.5,50.5,26) rot=(0.57735,-0.57735,-0.57735;4.18879rad)
  Tool = -> Cylinder030
FEATURE [Part::Cut] Cut027
  Base = -> Cut018
  Placement = pos=(-113.8,-33.8,26) rot=(0.57735,0.57735,-0.57735;2.0944rad)
  Tool = -> Cylinder030
FEATURE [Part::Cut] Cut028
  Base = -> Cut018
  Placement = pos=(-113.8,54.6,75.9572) rot=(0.57735,0.57735,-0.57735;2.0944rad)
  Tool = -> Cylinder030
FEATURE [Part::Cut] Cut029
  Base = -> Cut018
  Placement = pos=(-113.8,-45.5244,76) rot=(0.57735,0.57735,-0.57735;2.0944rad)
  Tool = -> Cylinder030
FEATURE [Part::Cut] Cut030
  Base = -> Cut018
  Placement = pos=(-6.72542,45.23,76) rot=(0.57735,-0.57735,-0.57735;4.18879rad)
  Tool = -> Cylinder030
FEATURE [Part::Cut] Cut031
  Base = -> Cut018
  Placement = pos=(-6.2,-55.7,76) rot=(0.57735,-0.57735,-0.57735;4.18879rad)
  Tool = -> Cylinder030
FEATURE [Part::Cut] Cut032
  Base = -> Cut018
  Placement = pos=(-56.7371,44.4421,126) rot=(0.57735,-0.57735,-0.57735;4.18879rad)
  Tool = -> Cylinder030
FEATURE [Part::Cut] Cut033
  Base = -> Cut018
  Placement = pos=(-55.7549,-55.4537,126) rot=(0.57735,-0.57735,-0.57735;4.18879rad)
  Tool = -> Cylinder030
FEATURE [Part::Cut] Cut034
  Base = -> Cut018
  Placement = pos=(-114.175,-34.5899,126) rot=(0.57735,0.57735,-0.57735;2.0944rad)
  Tool = -> Cylinder030
FEATURE [Part::Cut] Cut035
  Base = -> Cut018
  Placement = pos=(-113.675,44.2743,126) rot=(0.57735,0.57735,-0.57735;2.0944rad)
  Tool = -> Cylinder030
FEATURE [App::DocumentObjectGroup] Group006  label="flor0"
  Group = -> [Cut027,Cut026,Cut025,Cut024]
FEATURE [App::DocumentObjectGroup] Group007  label="flor1"
  Group = -> [Cut028,Cut029,Cut030,Cut031]
FEATURE [App::DocumentObjectGroup] Group008  label="flor2"
  Group = -> [Cut032,Cut033,Cut034,Cut035]
FEATURE [Sketcher::SketchObject] Sketch008  label="gropper"
  sketch-geometry (24):
    g0: LineSegment StartX=80.2034 StartY=30.1452 StartZ=0 EndX=100.11 EndY=30.1452 EndZ=0
    g1: LineSegment StartX=100.216 StartY=-30.1776 StartZ=0 EndX=80.2034 EndY=-30.1776 EndZ=0
    g2: LineSegment StartX=80.2034 StartY=-30.1776 StartZ=0 EndX=80.2034 EndY=30.1452 EndZ=0
    g3: LineSegment StartX=139.974 StartY=29.5055 StartZ=0 EndX=139.974 EndY=19.9512 EndZ=0
    g4: LineSegment StartX=139.709 StartY=-20.0089 StartZ=0 EndX=140.068 EndY=-29.5025 EndZ=0
    g5: LineSegment StartX=125.379 StartY=27.6382 StartZ=0 EndX=129.678 EndY=30.5041 EndZ=0
    g6: LineSegment StartX=129.678 StartY=30.5041 StartZ=0 EndX=134.515 EndY=27.6382 EndZ=0
    g7: LineSegment StartX=134.515 StartY=27.6382 StartZ=0 EndX=135.589 EndY=22.4435 EndZ=0
    g8: LineSegment StartX=135.589 StartY=22.4435 StartZ=0 EndX=139.974 EndY=19.9512 EndZ=0
    g9: LineSegment StartX=124.663 StartY=-27.7113 StartZ=0 EndX=128.962 EndY=-31.1146 EndZ=0
    g10: LineSegment StartX=128.962 StartY=-31.1146 StartZ=0 EndX=133.619 EndY=-28.4278 EndZ=0
    g11: LineSegment StartX=133.619 StartY=-28.4278 StartZ=0 EndX=135.052 EndY=-22.8749 EndZ=0
    g12: LineSegment StartX=135.052 StartY=-22.8749 StartZ=0 EndX=139.709 EndY=-20.0089 EndZ=0
    g13: LineSegment StartX=100.11 StartY=30.1452 StartZ=0 EndX=100.11 EndY=26.5496 EndZ=0
    g14: LineSegment StartX=100.149 StartY=16.1353 StartZ=0 EndX=100.149 EndY=-17.1102 EndZ=0
    g15: LineSegment StartX=100.216 StartY=-30.1776 StartZ=0 EndX=100.216 EndY=-26.8315 EndZ=0
    g16: LineSegment StartX=100.11 StartY=26.5496 StartZ=0 EndX=120.202 EndY=39.9887 EndZ=0
    g17: LineSegment StartX=120.269 StartY=29.7499 StartZ=0 EndX=100.149 EndY=16.1353 EndZ=0
    g18: LineSegment StartX=119.814 StartY=-30.0538 StartZ=0 EndX=100.149 EndY=-17.1102 EndZ=0
    g19: LineSegment StartX=100.216 StartY=-26.8315 StartZ=0 EndX=119.826 EndY=-39.8917 EndZ=0
    g20: LineSegment StartX=120.202 StartY=39.9887 StartZ=0 EndX=139.974 EndY=29.5055 EndZ=0
    g21: LineSegment StartX=120.269 StartY=29.7499 StartZ=0 EndX=125.379 EndY=27.6382 EndZ=0
    g22: LineSegment StartX=119.814 StartY=-30.0538 StartZ=0 EndX=124.663 EndY=-27.7113 EndZ=0
    g23: LineSegment StartX=119.826 StartY=-39.8917 StartZ=0 EndX=140.068 EndY=-29.5025 EndZ=0
  constraints (30):
    c: Coincident(g1,g2)
    c: Coincident(g2,g0)
    c: Horizontal(g0)
    c: Horizontal(g1)
    c: Vertical(g2)
    c: Coincident(g5,g6)
    c: Coincident(g6,g7)
    c: Coincident(g7,g8)
    c: Coincident(g8,g3)
    c: Coincident(g9,g10)
    c: Coincident(g10,g11)
    c: Coincident(g11,g12)
    c: Coincident(g12,g4)
    c: Coincident(g13,g0)
    c: Vertical(g13)
    c: Vertical(g14)
    c: Coincident(g15,g1)
    c: Vertical(g15)
    c: Coincident(g16,g13)
    c: Coincident(g17,g14)
    c: Coincident(g18,g14)
    c: Coincident(g19,g15)
    c: Coincident(g20,g16)
    c: Coincident(g20,g3)
    c: Coincident(g21,g17)
    c: Coincident(g21,g5)
    c: Coincident(g22,g18)
    c: Coincident(g22,g9)
    c: Coincident(g23,g19)
    c: Coincident(g23,g4)
FEATURE [PartDesign::Pad] Pad007  label="gripper"
  Length = 10
  MirroredExtent = false
  Sketch = -> Sketch008
FEATURE [Part::Box] Box001
  Height = 87
  Length = 80
  Placement = pos=(-50,26,251.5) rot=(0,1,0;3.14159rad)
  Width = 110
FEATURE [Sketcher::SketchObject] Sketch009
  sketch-geometry (11):
    g0: LineSegment StartX=-120.266 StartY=55.8702 StartZ=0 EndX=-120.266 EndY=-35.2585 EndZ=0
    g1: LineSegment StartX=-120.266 StartY=-35.2585 StartZ=0 EndX=-50.1957 EndY=-35.2585 EndZ=0
    g2: LineSegment StartX=-50.1957 StartY=-35.2585 StartZ=0 EndX=-50.319 EndY=-25.484 EndZ=0
    g3: LineSegment StartX=-50.319 StartY=-25.484 StartZ=0 EndX=-57.7715 EndY=-25.484 EndZ=0
    g4: LineSegment StartX=-65.5367 StartY=-29.5767 StartZ=0 EndX=-109.382 EndY=30.4233 EndZ=0
    g5: LineSegment StartX=-109.382 StartY=30.4233 StartZ=0 EndX=-109.382 EndY=39.9073 EndZ=0
    g6: LineSegment StartX=-109.382 StartY=39.9073 StartZ=0 EndX=-100.312 EndY=39.9073 EndZ=0
    g7: LineSegment StartX=-100.312 StartY=39.9073 StartZ=0 EndX=-100.312 EndY=55.8702 EndZ=0
    g8: LineSegment StartX=-100.312 StartY=55.8702 StartZ=0 EndX=-120.266 EndY=55.8702 EndZ=0
    g9: LineSegment StartX=-65.5367 StartY=-29.5767 StartZ=0 EndX=-57.7715 EndY=-29.5767 EndZ=0
    g10: LineSegment StartX=-57.7715 StartY=-29.5767 StartZ=0 EndX=-57.7715 EndY=-25.484 EndZ=0
  constraints (20):
    c: Vertical(g0)
    c: Coincident(g0,g1)
    c: Horizontal(g1)
    c: Coincident(g1,g2)
    c: Coincident(g2,g3)
    c: Coincident(g4,g5)
    c: Vertical(g5)
    c: Coincident(g5,g6)
    c: Horizontal(g6)
    c: Coincident(g6,g7)
    c: Vertical(g7)
    c: Coincident(g7,g8)
    c: Coincident(g8,g0)
    c: Horizontal(g8)
    c: DistanceY(g4) = 60
    c: Coincident(g9,g4)
    c: Horizontal(g9)
    c: Coincident(g10,g9)
    c: Coincident(g10,g3)
    c: Horizontal(g3)
FEATURE [PartDesign::Pad] Pad008
  Length = 130
  MirroredExtent = false
  Placement = pos=(-1.15663,146.081,200.7) rot=(1,0,0;1.5708rad)
  Sketch = -> Sketch009
FEATURE [Part::Cut] Cut036
  Base = -> Pad008
  Placement = pos=(0.470886,-81.3035,-10.7339) rot=(0,0,1;0rad)
  Tool = -> Box001
FEATURE [Sketcher::SketchObject] Sketch010
  sketch-geometry (4):
    g0: LineSegment StartX=-125.009 StartY=156.743 StartZ=0 EndX=-50.0091 EndY=156.743 EndZ=0
    g1: LineSegment StartX=-50.0091 StartY=156.743 StartZ=0 EndX=-50.0091 EndY=36.7431 EndZ=0
    g2: LineSegment StartX=-50.0091 StartY=36.7431 StartZ=0 EndX=-125.009 EndY=36.7431 EndZ=0
    g3: LineSegment StartX=-125.009 StartY=36.7431 StartZ=0 EndX=-125.009 EndY=156.743 EndZ=0
  constraints (10):
    c: Coincident(g0,g1)
    c: Coincident(g1,g2)
    c: Coincident(g2,g3)
    c: Coincident(g3,g0)
    c: Horizontal(g0)
    c: Horizontal(g2)
    c: Vertical(g1)
    c: Vertical(g3)
    c: DistanceY(g3) = 120
    c: DistanceX(g0) = 75
FEATURE [PartDesign::Pad] Pad009
  Length = 10
  MirroredExtent = false
  Sketch = -> Sketch010
FEATURE [Part::Box] Box002
  Height = 10
  Length = 55
  Placement = pos=(-115,45.8,7.5) rot=(0,0,1;0rad)
  Width = 100
FEATURE [Part::Cut] Cut037  label="display"
  Base = -> Pad009
  Placement = pos=(-34.7923,-97.0035,121.476) rot=(0,1,0;0.928855rad)
  Tool = -> Box002
FEATURE [Part::Box] Box003
  Height = 23
  Length = 23
  Placement = pos=(28.3401,28.6705,-9.64305) rot=(0,0,1;0rad)
  Width = 12
FEATURE [Part::Box] Box004
  Height = 1.7
  Length = 32
  Placement = pos=(24.15,28.6705,7.9668) rot=(0,0,1;0rad)
  Width = 12
FEATURE [Part::Cylinder] Cylinder032
  Angle = 360
  Height = 10
  Placement = pos=(53.8219,34.6,2.58368) rot=(0,0,1;0rad)
  Radius = 1
FEATURE [Part::Cylinder] Cylinder034
  Angle = 360
  Height = 10
  Placement = pos=(26.1112,34.5,1.79316) rot=(0,0,1;0rad)
  Radius = 1
FEATURE [Part::MultiFuse] Fusion003
  Shapes = -> [Box004,Box003]
FEATURE [Part::Cut] Cut038
  Base = -> Fusion003
  Tool = -> Cylinder034
FEATURE [Part::Cut] Cut039
  Base = -> Cut038
  Tool = -> Cylinder032
FEATURE [Part::Cylinder] Cylinder035
  Angle = 360
  Height = 10
  Placement = pos=(41.2515,34.4472,6.56) rot=(0,0,1;0rad)
  Radius = 2
FEATURE [Part::Cylinder] Cylinder036
  Angle = 360
  Height = 10
  Placement = pos=(34.4857,34.67,6.56) rot=(0,0,1;0rad)
  Radius = 6
FEATURE [Part::Box] Box005
  Height = 1.5
  Length = 37
  Width = 4.5
FEATURE [Part::Box] Box006
  Height = 1.5
  Length = 17
  Placement = pos=(20.2342,-6.49055,0) rot=(0,0,1;1.5708rad)
  Width = 4.5
FEATURE [Part::MultiFuse] Fusion004
  Placement = pos=(16.4876,32.0839,17.56) rot=(0,0,1;0rad)
  Shapes = -> [Box006,Box005]
FEATURE [Part::Cylinder] Cylinder037
  Angle = 360
  Height = 10
  Placement = pos=(34.5,34.5,10.7594) rot=(0,0,1;0rad)
  Radius = 2
FEATURE [Part::MultiFuse] Fusion005
  Placement = pos=(-49,17.44,105.53) rot=(0.57735,0.57735,-0.57735;2.0944rad)
  Shapes = -> [Cylinder035,Cylinder036,Cut039]
FEATURE [Part::MultiFuse] Fusion006
  Placement = pos=(-48.6,17.44,105.53) rot=(0.57735,0.57735,-0.57735;2.0944rad)
  Shapes = -> [Fusion004,Cylinder037]
FEATURE [Sketcher::SketchObject] Sketch011
  sketch-geometry (12):
    g0: LineSegment StartX=-95.0946 StartY=32.3618 StartZ=0 EndX=-60.0946 EndY=32.3618 EndZ=0
    g1: LineSegment StartX=-59.724 StartY=-12.6382 StartZ=0 EndX=-95.0946 EndY=-12.6382 EndZ=0
    g2: LineSegment StartX=-95.0946 StartY=-12.6382 StartZ=0 EndX=-95.0946 EndY=32.3618 EndZ=0
    g3: LineSegment StartX=-60.0946 StartY=15.2279 StartZ=0 EndX=-29.8289 EndY=15.2279 EndZ=0
    g4: LineSegment StartX=-29.8289 StartY=15.2279 StartZ=0 EndX=-29.8289 EndY=5.22794 EndZ=0
    g5: LineSegment StartX=-29.8289 StartY=5.22794 StartZ=0 EndX=-59.724 EndY=5.22794 EndZ=0
    g6: LineSegment StartX=-59.724 StartY=-12.6382 StartZ=0 EndX=-59.724 EndY=5.22794 EndZ=0
    g7: LineSegment StartX=-60.0946 StartY=15.2279 StartZ=0 EndX=-60.0946 EndY=32.3618 EndZ=0
    g8: LineSegment StartX=-82.1826 StartY=15.2164 StartZ=0 EndX=-72.1826 EndY=15.2164 EndZ=0
    g9: LineSegment StartX=-72.1826 StartY=15.2164 StartZ=0 EndX=-72.1826 EndY=5.21644 EndZ=0
    g10: LineSegment StartX=-72.1826 StartY=5.21644 StartZ=0 EndX=-82.1826 EndY=5.21644 EndZ=0
    g11: LineSegment StartX=-82.1826 StartY=5.21644 StartZ=0 EndX=-82.1826 EndY=15.2164 EndZ=0
  constraints (29):
    c: Coincident(g1,g2)
    c: Coincident(g2,g0)
    c: Horizontal(g0)
    c: Horizontal(g1)
    c: Vertical(g2)
    c: Coincident(g3,g4)
    c: Coincident(g4,g5)
    c: Horizontal(g3)
    c: Horizontal(g5)
    c: Vertical(g4)
    c: Coincident(g6,g1)
    c: Coincident(g6,g5)
    c: Vertical(g6)
    c: Coincident(g7,g3)
    c: Coincident(g7,g0)
    c: Vertical(g7)
    c: DistanceY(g4) = -10
    c: Coincident(g8,g9)
    c: Coincident(g9,g10)
    c: Coincident(g10,g11)
    c: Coincident(g11,g8)
    c: Horizontal(g8)
    c: Horizontal(g10)
    c: Vertical(g9)
    c: Vertical(g11)
    c: DistanceY(g2) = 45
    c: DistanceX(g0) = 35
    c: DistanceY(g9) = -10
    c: DistanceX(g8) = 10
FEATURE [PartDesign::Pad] Pad010  label="camera_Pad"
  Length = 4
  MirroredExtent = false
  Placement = pos=(-16.3,-10.67,50) rot=(0,1,0;1.5708rad)
  Sketch = -> Sketch011
FEATURE [App::DocumentObjectGroup] Group009  label="micro_servo"
  Group = -> [Fusion006,Fusion005,Pad010]
FEATURE [Part::Feature] RaspBerry
  Placement = pos=(-12.8029,-1.75778,11.0436) rot=(1,0,0;1.5708rad)
  shape: bbox 85.6 x 53.98 x 1.35 mm, 6 faces (baked)
FEATURE [Part::Feature] RaspBerry001
  Placement = pos=(-55.5029,-21.2478,13.6186) rot=(0.57735,-0.57735,-0.57735;2.0944rad)
  shape: bbox 5.461 x 7.999 x 2.949 mm, 809 faces (baked)
FEATURE [Part::Feature] RaspBerry002
  Placement = pos=(-50.8029,-21.2478,13.6186) rot=(0.57735,-0.57735,-0.57735;2.0944rad)
  shape: bbox 3.937 x 6.982 x 2.155 mm, 206 faces (baked)
FEATURE [Part::Feature] RaspBerry003 .. RaspBerry007  x5 (patterned run collapsed; names and placements below)
  shape: bbox 4 x 0.37 x 1.716 mm, 43 faces (baked)
  placements: all 5 at pos=(-50.8029,-21.2478,13.6186) rot=(0.57735,-0.57735,-0.57735;2.0944rad)
FEATURE [Part::Feature] RaspBerry008
  Placement = pos=(-11.3429,-29.2478,15.6986) rot=(1,0,0;1.5708rad)
  shape: bbox 15 x 12 x 8.275 mm, 506 faces (baked)
FEATURE [Part::Feature] RaspBerry009
  Placement = pos=(31.4971,-18.8103,18.9976) rot=(0.57735,0.57735,0.57735;2.0944rad)
  shape: bbox 20.57 x 17.91 x 14.48 mm, 219 faces (baked)
FEATURE [Part::Feature] RaspBerry010
  Placement = pos=(-55.0129,-0.297781,11.0436) rot=(0.57735,0.57735,-0.57735;4.18879rad)
  shape: bbox 3 x 0.7 x 1.3 mm, 115 faces (baked)
FEATURE [Part::Feature] RaspBerry011
  Placement = pos=(-55.0129,-0.297781,11.0436) rot=(0.57735,0.57735,-0.57735;4.18879rad)
  shape: bbox 32.12 x 24.12 x 2.1 mm, 97 faces (baked)
FEATURE [Part::Feature] RaspBerry012
  Placement = pos=(-55.0129,-0.297781,11.0436) rot=(0.57735,0.57735,-0.57735;4.18879rad)
  shape: bbox 4.8 x 1.9 x 0.1 mm, 6 faces (baked)
FEATURE [Part::Feature] RaspBerry013
  Placement = pos=(-55.0129,-0.297781,11.0436) rot=(0.57735,0.57735,-0.57735;4.18879rad)
  shape: bbox 4.8 x 1.9 x 0.1 mm, 6 faces (baked)
FEATURE [Part::Feature] RaspBerry014
  Placement = pos=(-55.0129,-0.297781,11.0436) rot=(0.57735,0.57735,-0.57735;4.18879rad)
  shape: bbox 5.9 x 1.9 x 0.1 mm, 6 faces (baked)
FEATURE [Part::Feature] RaspBerry015
  Placement = pos=(-55.0129,-0.297781,11.0436) rot=(0.57735,0.57735,-0.57735;4.18879rad)
  shape: bbox 5.9 x 1.9 x 0.1 mm, 6 faces (baked)
FEATURE [Part::Feature] RaspBerry016
  Placement = pos=(-55.0129,-0.297781,11.0436) rot=(0.57735,0.57735,-0.57735;4.18879rad)
  shape: bbox 4.8 x 1.9 x 0.1 mm, 6 faces (baked)
FEATURE [Part::Feature] RaspBerry017
  Placement = pos=(-55.0129,-0.297781,11.0436) rot=(0.57735,0.57735,-0.57735;4.18879rad)
  shape: bbox 4.8 x 1.9 x 0.1 mm, 6 faces (baked)
FEATURE [Part::Feature] RaspBerry018
  Placement = pos=(-55.0129,-0.297781,11.0436) rot=(0.57735,0.57735,-0.57735;4.18879rad)
  shape: bbox 4.8 x 3.6 x 0.1 mm, 10 faces (baked)
FEATURE [Part::Feature] RaspBerry019
  Placement = pos=(-55.0129,-0.297781,11.0436) rot=(0.57735,0.57735,-0.57735;4.18879rad)
  shape: bbox 6.819 x 1.9 x 0.1 mm, 9 faces (baked)
FEATURE [Part::Feature] RaspBerry020
  Placement = pos=(9.36709,22.2322,12.3936) rot=(0.57735,-0.57735,-0.57735;2.0944rad)
  shape: bbox 12 x 15 x 10.79 mm, 46 faces (baked)
FEATURE [Part::Feature] RaspBerry021 .. RaspBerry024  x4 (patterned run collapsed; names and placements below)
  shape: bbox 1.145 x 2 x 7.071 mm, 28 faces (baked)
  placements: all 4 at pos=(9.36709,22.2322,12.3936) rot=(0.57735,-0.57735,-0.57735;2.0944rad)
FEATURE [Part::Feature] RaspBerry025
  Placement = pos=(9.36709,22.2322,12.3936) rot=(0.57735,-0.57735,-0.57735;2.0944rad)
  shape: bbox 0.5 x 1.364 x 4.133 mm, 25 faces (baked)
FEATURE [Part::Feature] RaspBerry026
  Placement = pos=(26.4971,1.80222,17.6636) rot=(0.57735,0.57735,0.57735;2.0944rad)
  shape: bbox 17.1 x 13.1 x 15.62 mm, 56 faces (baked)
FEATURE [Part::Feature] RaspBerry027
  Placement = pos=(-8.00671,22.7322,12.3936) rot=(0,0.707107,0.707107;3.14159rad)
  shape: bbox 10.01 x 19.51 x 16.99 mm, 72 faces (baked)
FEATURE [Part::Feature] RaspBerry028
  Placement = pos=(-15.6029,-2.76778,12.3936) rot=(0,0,1;0rad)
  shape: bbox 12 x 12 x 1.4 mm, 6 faces (baked)
FEATURE [Part::Feature] RaspBerry029 .. RaspBerry036  x8 (patterned run collapsed; names and placements below)
  shape: bbox 2.54 x 2.54 x 12.19 mm, 32 faces (baked)
  placements: 8 in arithmetic series — first pos=(-1.27291,14.9622,12.3936) rot=(0,0,1;0rad), step (0,-2.5,0), last pos=(-1.27291,-2.53778,12.3936) rot=(0,0,1;0rad)
FEATURE [Part::Feature] RaspBerry037 .. RaspBerry048  x12 (patterned run collapsed; names and placements below)
  shape: bbox 5.08 x 5.08 x 12.19 mm, 116 faces (baked)
  placements: 12 in arithmetic series — first pos=(-53.3329,20.4222,12.3936) rot=(0,0,1;0rad), step (2.5,0,0), last pos=(-25.8329,20.4222,12.3936) rot=(0,0,1;0rad)
FEATURE [Part::Feature] RaspBerry049
  Placement = pos=(-37.8129,-0.197781,10.9436) rot=(-0.57735,-0.57735,0.57735;2.0944rad)
  shape: bbox 18.89 x 28 x 3.8 mm, 190 faces (baked)
FEATURE [Part::Feature] RaspBerry050
  Placement = pos=(-42.3029,-21.6478,12.3936) rot=(1,0,0;1.5708rad)
  shape: bbox 6.819 x 6.819 x 7.7 mm, 13 faces (baked)
FEATURE [Part::Feature] RaspBerry051
  Placement = pos=(5.53377,-6.74778,12.3936) rot=(0.57735,0.57735,0.57735;2.0944rad)
  shape: bbox 2.6 x 22 x 5.9 mm, 15 faces (baked)
FEATURE [Part::Feature] RaspBerry052
  Placement = pos=(-45.1029,-13.7678,12.3936) rot=(0.57735,-0.57735,-0.57735;2.0944rad)
  shape: bbox 2.6 x 22 x 5.9 mm, 15 faces (baked)
FEATURE [App::DocumentObjectGroup] Group010  label="RPi"
  Group = -> [RaspBerry,RaspBerry002,RaspBerry004,RaspBerry006,RaspBerry008,RaspBerry010,RaspBerry012,RaspBerry014,RaspBerry016,RaspBerry018,RaspBerry020,RaspBerry022,RaspBerry024,RaspBerry026,RaspBerry028,RaspBerry030,RaspBerry032,RaspBerry034,RaspBerry036,RaspBerry038,RaspBerry040,RaspBerry042,RaspBerry044,RaspBerry046,RaspBerry048,RaspBerry050,RaspBerry052,RaspBerry005,RaspBerry009,RaspBerry013,RaspBerry017,+22 more]
FEATURE [Mesh::Feature] rpi_arduino_robot
  Placement = pos=(-14,-4.5,22) rot=(0,0,1;0rad)
